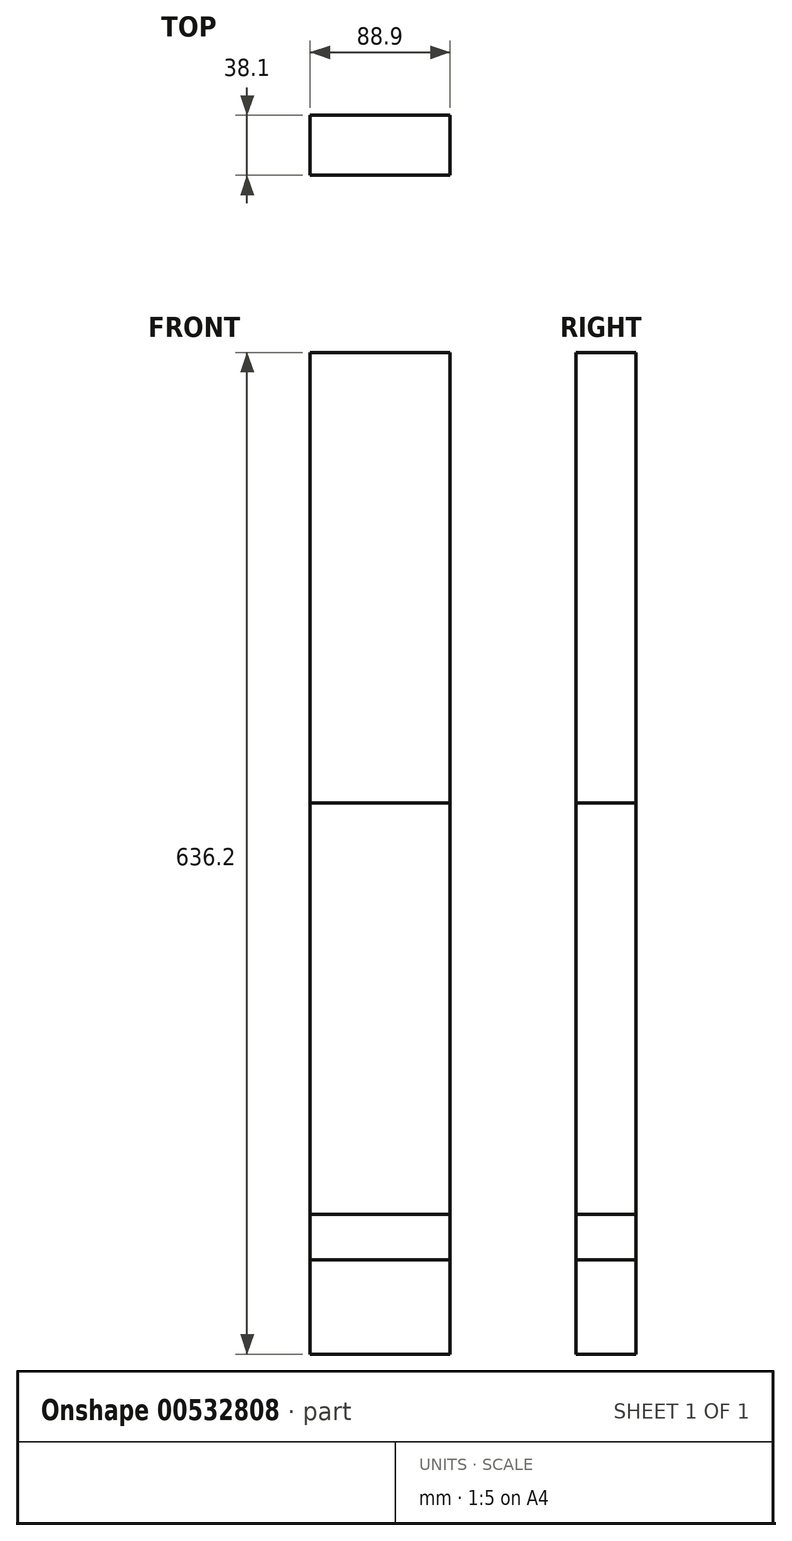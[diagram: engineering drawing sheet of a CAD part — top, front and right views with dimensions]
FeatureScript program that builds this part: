
annotation { "Feature Type Name" : "Feature", "Feature Type Description" : "" }
export const myFeature = defineFeature(function(context is Context, id is Id, definition is map)
    precondition{}
    {
        {
            var Q0;
            Q0=qCreatedBy(makeId("Top.planeOp"),FACE);
            var sketch = newSketch(context, id + "F0", { "sketchPlane" : qUnion([Q0])});
            skLineSegment(sketch, "E0.bottom", {"start": v(-44.45, 19.05) * mm, "end": v(44.45, 19.05) * mm});
            skLineSegment(sketch, "E0.top", {"start": v(-44.45, -19.05) * mm, "end": v(44.45, -19.05) * mm});
            skLineSegment(sketch, "E0.left", {"start": v(-44.45, 19.05) * mm, "end": v(-44.45, -19.05) * mm});
            skLineSegment(sketch, "E0.right", {"start": v(44.45, 19.05) * mm, "end": v(44.45, -19.05) * mm});
            skPoint(sketch, "E0.middle", {"position": v(0, 0) * mm});
            skSolve(sketch);
        }
        {
            var Q0;
            Q0=makeQuery(id+"F0.imprint","IMPRINT",FACE,{"disambiguationData":[TD([[makeQuery(id+"F0.imprint","IMPRINT",EDGE,{"derivedFrom":sQuery(id+"F0.wireOp",EDGE,"E0.bottom")}),-1.0]])]});
            extrude(context, id + "F1", {"entities" : qUnion([Q0]), "depth" : 350 * mm, "offsetDistance" : 25.4 * mm});
        }
        {
            var Q0;
            Q0=makeQuery(id+"F0.imprint","IMPRINT",FACE,{"disambiguationData":[TD([[makeQuery(id+"F0.imprint","IMPRINT",EDGE,{"derivedFrom":sQuery(id+"F0.wireOp",EDGE,"E0.bottom")}),-1.0]])]});
            extrude(context, id + "F2", {"entities" : qUnion([Q0]), "depth" : 636.2 * mm, "offsetDistance" : 25.4 * mm});
        }
        {
            var Q0;
            Q0=makeQuery(id+"F0.imprint","IMPRINT",FACE,{"disambiguationData":[TD([[makeQuery(id+"F0.imprint","IMPRINT",EDGE,{"derivedFrom":sQuery(id+"F0.wireOp",EDGE,"E0.bottom")}),-1.0]])]});
            extrude(context, id + "F3", {"entities" : qUnion([Q0]), "depth" : 88.9 * mm, "offsetDistance" : 25.4 * mm});
        }
        {
            var Q0;
            Q0=makeQuery(id+"F0.imprint","IMPRINT",FACE,{"disambiguationData":[TD([[makeQuery(id+"F0.imprint","IMPRINT",EDGE,{"derivedFrom":sQuery(id+"F0.wireOp",EDGE,"E0.bottom")}),-1.0]])]});
            extrude(context, id + "F4", {"entities" : qUnion([Q0]), "depth" : 60 * mm, "offsetDistance" : 25.4 * mm});
        }
    });
